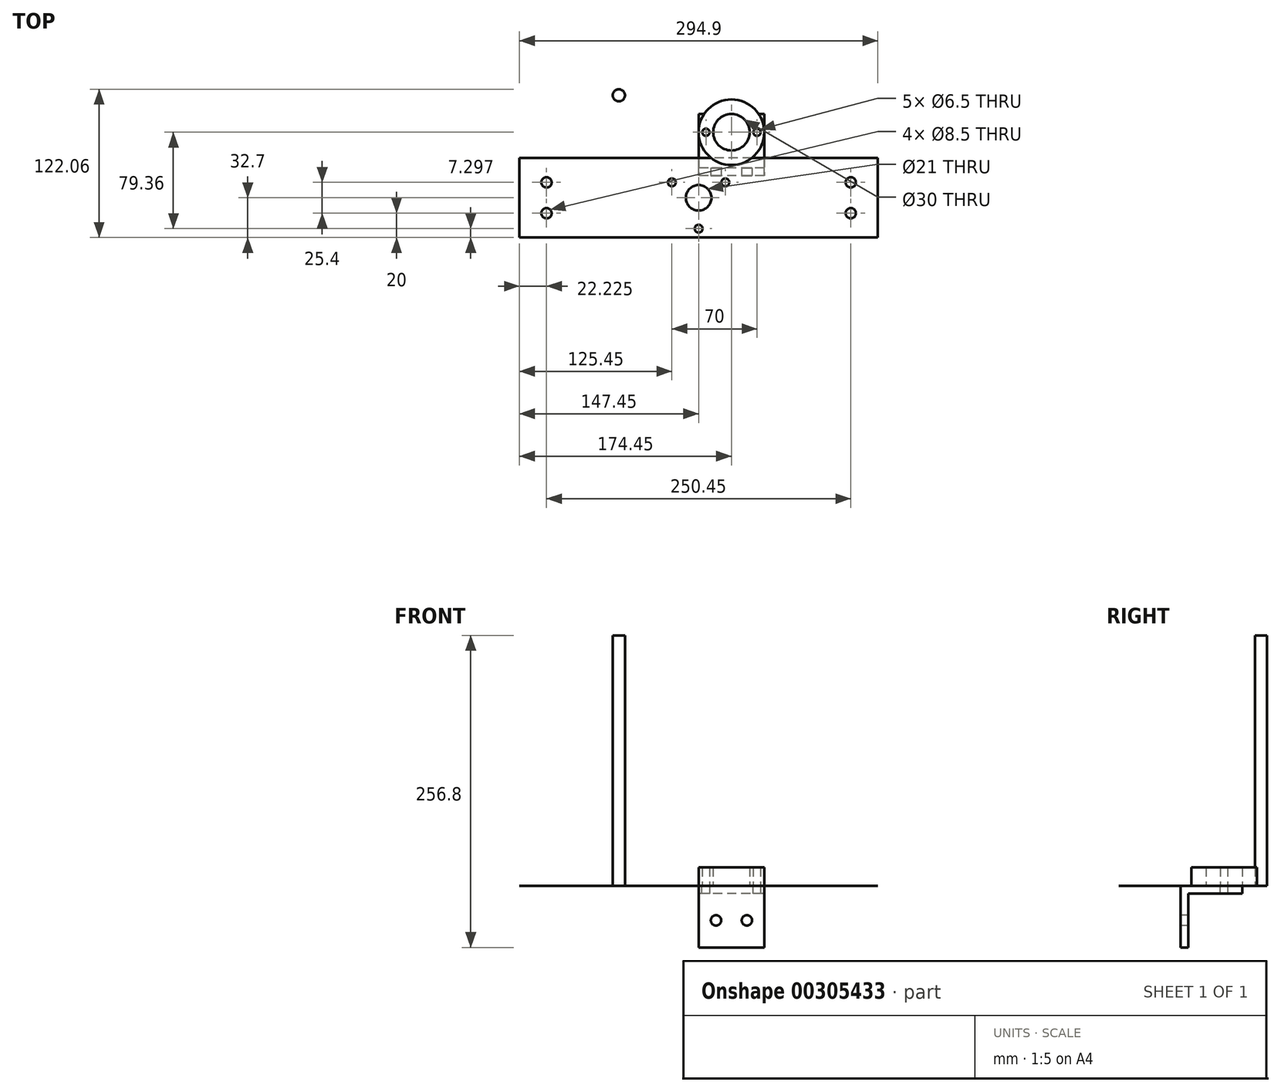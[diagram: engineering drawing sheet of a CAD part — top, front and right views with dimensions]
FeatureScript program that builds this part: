
annotation { "Feature Type Name" : "Feature", "Feature Type Description" : "" }
export const myFeature = defineFeature(function(context is Context, id is Id, definition is map)
    precondition{}
    {
        {
            var Q0;
            Q0=qCreatedBy(makeId("Top.planeOp"),FACE);
            var sketch = newSketch(context, id + "F0", { "sketchPlane" : qUnion([Q0])});
            skCircle(sketch, "E0", {"center": v(0, 0) * mm, "radius": 10.5 * mm});
            skLineSegment(sketch, "E1", {"start": v(-22, 12.7) * mm, "end": v(22, 12.7) * mm, "construction": true});
            skLineSegment(sketch, "E2", {"start": v(0, 12.7) * mm, "end": v(0, 0) * mm, "construction": true});
            skLineSegment(sketch, "E3", {"start": v(22, 12.7) * mm, "end": v(0, -25.4) * mm, "construction": true});
            skLineSegment(sketch, "E4", {"start": v(11, -6.35) * mm, "end": v(0, 0) * mm, "construction": true});
            skLineSegment(sketch, "E5", {"start": v(-22, 12.7) * mm, "end": v(0, -25.4) * mm, "construction": true});
            skLineSegment(sketch, "E6", {"start": v(-11, -6.35) * mm, "end": v(0, 0) * mm, "construction": true});
            skCircle(sketch, "E7", {"center": v(-22, 12.7) * mm, "radius": 3.25 * mm});
            skCircle(sketch, "E8", {"center": v(22, 12.7) * mm, "radius": 3.25 * mm});
            skCircle(sketch, "E9", {"center": v(0, -25.4) * mm, "radius": 3.25 * mm});
            skLineSegment(sketch, "E10.bottom", {"start": v(147.45, -32.7) * mm, "end": v(-147.45, -32.7) * mm});
            skLineSegment(sketch, "E10.top", {"start": v(147.45, 32.7) * mm, "end": v(-147.45, 32.7) * mm});
            skLineSegment(sketch, "E10.left", {"start": v(147.45, -32.7) * mm, "end": v(147.45, 32.7) * mm});
            skLineSegment(sketch, "E10.right", {"start": v(-147.45, -32.7) * mm, "end": v(-147.45, 32.7) * mm});
            skCircle(sketch, "E11", {"center": v(-125.23, 12.7) * mm, "radius": 4.25 * mm});
            skCircle(sketch, "E12", {"center": v(-125.23, -12.7) * mm, "radius": 4.25 * mm});
            skCircle(sketch, "E13", {"center": v(125.23, 12.7) * mm, "radius": 4.25 * mm});
            skCircle(sketch, "E14", {"center": v(125.23, -12.7) * mm, "radius": 4.25 * mm});
            skPoint(sketch, "E15", {"position": v(-103, 32.7) * mm});
            skPoint(sketch, "E16", {"position": v(103, 32.7) * mm});
            skPoint(sketch, "E17", {"position": v(-125.23, 32.7) * mm});
            skPoint(sketch, "E18", {"position": v(125.23, 32.7) * mm});
            skSolve(sketch);
        }
        {
            var Q0;
            Q0=qCreatedBy(makeId("Top.planeOp"),FACE);
            var sketch = newSketch(context, id + "F1", { "sketchPlane" : qUnion([Q0])});
            skCircle(sketch, "E19", {"center": v(27, 53.96) * mm, "radius": 15 * mm});
            skCircle(sketch, "E20", {"center": v(27, 53.96) * mm, "radius": 27 * mm});
            skCircle(sketch, "E21", {"center": v(6, 53.96) * mm, "radius": 3 * mm});
            skCircle(sketch, "E22", {"center": v(48, 53.96) * mm, "radius": 3 * mm});
            skPoint(sketch, "E23", {"position": v(0, 53.96) * mm});
            skSolve(sketch);
        }
        {
            var Q0;
            Q0=makeQuery(id+"F1.imprint","IMPRINT",FACE,{"disambiguationData":[TD([[makeQuery(id+"F1.imprint","IMPRINT",EDGE,{"derivedFrom":sQuery(id+"F1.wireOp",EDGE,"E19")}),-1.0]])]});
            extrude(context, id + "F2", {"entities" : qUnion([Q0]), "depth" : 15 * mm});
        }
        {
            var Q0;
            Q0=qCreatedBy(makeId("Top.planeOp"),FACE);
            var sketch = newSketch(context, id + "F3", { "sketchPlane" : qUnion([Q0])});
            skCircle(sketch, "E24", {"center": v(-65.66, 84.36) * mm, "radius": 5 * mm});
            skSolve(sketch);
        }
        {
            var Q0;
            Q0=makeQuery(id+"F3.imprint","IMPRINT",FACE,{"disambiguationData":[TD([[makeQuery(id+"F3.imprint","IMPRINT",EDGE,{"derivedFrom":sQuery(id+"F3.wireOp",EDGE,"E24")}),1.0]])]});
            extrude(context, id + "F4", {"entities" : qUnion([Q0]), "depth" : 206 * mm});
        }
        {
            var Q0;
            Q0=qCreatedBy(makeId("Right.planeOp"),FACE);
            var sketch = newSketch(context, id + "F5", { "sketchPlane" : qUnion([Q0])});
            skPoint(sketch, "E25.0", {"position": v(53.96, 0) * mm});
            skLineSegment(sketch, "E26", {"start": v(68.96, 0) * mm, "end": v(18.16, 0) * mm});
            skLineSegment(sketch, "E27", {"start": v(18.16, 0) * mm, "end": v(18.16, -50.8) * mm});
            skLineSegment(sketch, "E28", {"start": v(18.16, -50.8) * mm, "end": v(24.5, -50.8) * mm});
            skLineSegment(sketch, "E29", {"start": v(24.5, -50.8) * mm, "end": v(24.5, -6.35) * mm});
            skLineSegment(sketch, "E30", {"start": v(24.5, -6.35) * mm, "end": v(68.96, -6.35) * mm});
            skLineSegment(sketch, "E31", {"start": v(68.96, -6.35) * mm, "end": v(68.96, 0) * mm});
            skSolve(sketch);
        }
        {
            var Q0;
            Q0=makeQuery(id+"F5.imprint","IMPRINT",FACE,{"disambiguationData":[TD([[makeQuery(id+"F5.imprint","IMPRINT",EDGE,{"derivedFrom":sQuery(id+"F5.wireOp",EDGE,"E26")}),1.0]])]});
            extrude(context, id + "F6", {"entities" : qUnion([Q0]), "depth" : 54 * mm});
        }
        {
            var Q0;
            Q0=makeQuery(id+"F6.opExtrude","SWEPT_FACE",FACE,{"disambiguationData":[OSD([sQuery(id+"F5.wireOp",EDGE,"E26")])]});
            var sketch = newSketch(context, id + "F7", { "sketchPlane" : qUnion([Q0])});
            skPoint(sketch, "E32.0", {"position": v(6, 53.96) * mm});
            skPoint(sketch, "E33.0", {"position": v(48, 53.96) * mm});
            skCircle(sketch, "E34", {"center": v(6, 53.96) * mm, "radius": 3.25 * mm});
            skCircle(sketch, "E35", {"center": v(48, 53.96) * mm, "radius": 3.25 * mm});
            skSolve(sketch);
        }
        {
            var Q0;
            Q0 = qSketchRegion(id + "F7", true);
            extrude(context, id + "F8", {"entities" : qUnion([Q0]), "operationType" : NewBodyOperationType.REMOVE, "oppositeDirection" : true, "depth" : 25 * mm});
        }
        {
            var Q0;
            Q0=makeQuery(id+"F6.opExtrude","SWEPT_FACE",FACE,{"disambiguationData":[OSD([sQuery(id+"F5.wireOp",EDGE,"E27")])]});
            var sketch = newSketch(context, id + "F9", { "sketchPlane" : qUnion([Q0])});
            skLineSegment(sketch, "E36.bottom", {"start": v(54, 0) * mm, "end": v(0, 0) * mm});
            skLineSegment(sketch, "E36.top", {"start": v(54, -50.8) * mm, "end": v(0, -50.8) * mm});
            skLineSegment(sketch, "E36.left", {"start": v(54, 0) * mm, "end": v(54, -50.8) * mm});
            skLineSegment(sketch, "E36.right", {"start": v(0, 0) * mm, "end": v(0, -50.8) * mm});
            skLineSegment(sketch, "E37", {"start": v(0, -6.35) * mm, "end": v(54, -6.35) * mm, "construction": true});
            skLineSegment(sketch, "E38", {"start": v(27, -6.35) * mm, "end": v(27, -50.8) * mm, "construction": true});
            skLineSegment(sketch, "E39", {"start": v(14.3, -28.57) * mm, "end": v(39.7, -28.57) * mm, "construction": true});
            skPoint(sketch, "E39.startSnap0", {"position": v(27, -28.57) * mm});
            skPoint(sketch, "E40", {"position": v(27, -28.58) * mm});
            skCircle(sketch, "E41", {"center": v(39.7, -28.57) * mm, "radius": 4.25 * mm});
            skCircle(sketch, "E42", {"center": v(14.3, -28.57) * mm, "radius": 4.25 * mm});
            skLineSegment(sketch, "E43", {"start": v(39.7, -28.57) * mm, "end": v(39.7, -50.8) * mm, "construction": true});
            skSolve(sketch);
        }
        {
            var Q0;
            Q0=makeQuery(id+"F9.imprint","IMPRINT",FACE,{"disambiguationData":[TD([[makeQuery(id+"F9.imprint","IMPRINT",EDGE,{"derivedFrom":sQuery(id+"F9.wireOp",EDGE,"E42")}),1.0]])]});
            var Q1;
            Q1=makeQuery(id+"F9.imprint","IMPRINT",FACE,{"disambiguationData":[TD([[makeQuery(id+"F9.imprint","IMPRINT",EDGE,{"derivedFrom":sQuery(id+"F9.wireOp",EDGE,"E41")}),1.0]])]});
            extrude(context, id + "F10", {"entities" : qUnion([Q0, Q1]), "operationType" : NewBodyOperationType.REMOVE, "oppositeDirection" : true, "depth" : 25 * mm});
        }
        {
            var Q0;
            Q0=makeQuery(id+"F0.imprint","IMPRINT",FACE,{"disambiguationData":[TD([[makeQuery(id+"F0.imprint","IMPRINT",EDGE,{"derivedFrom":sQuery(id+"F0.wireOp",EDGE,"E0")}),-1.0]])]});
            extrude(context, id + "F11", {"entities" : qUnion([Q0]), "depth" : 1 / 101.6 * mm});
        }
    });
